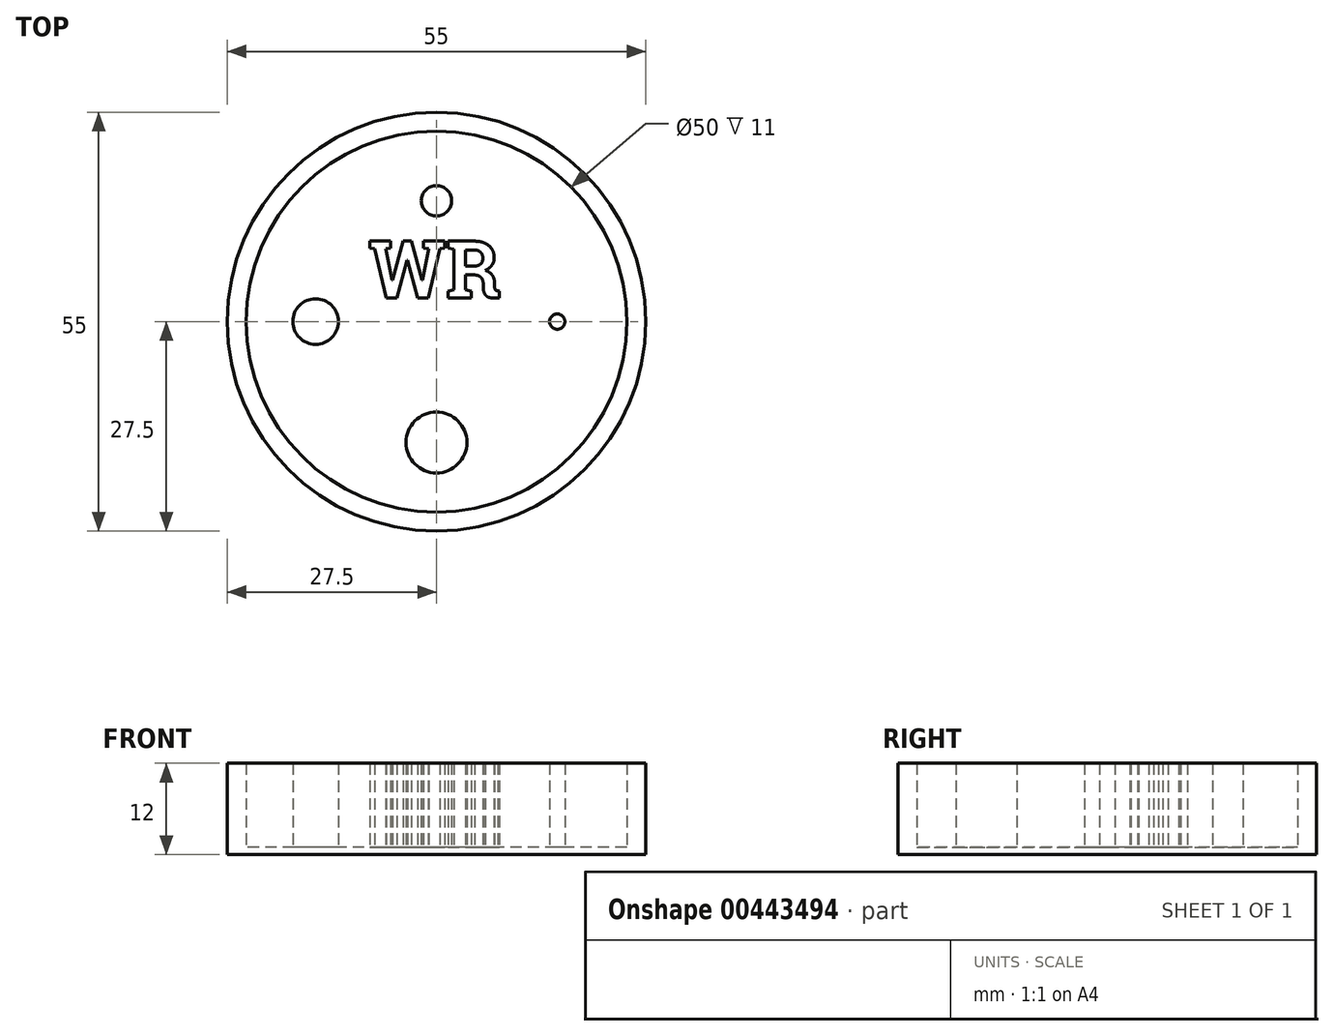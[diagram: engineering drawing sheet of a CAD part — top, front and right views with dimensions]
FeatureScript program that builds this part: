
annotation { "Feature Type Name" : "Feature", "Feature Type Description" : "" }
export const myFeature = defineFeature(function(context is Context, id is Id, definition is map)
    precondition{}
    {
        {
            var Q0;
            Q0=qCreatedBy(makeId("Top.planeOp"),FACE);
            var sketch = newSketch(context, id + "F0", { "sketchPlane" : qUnion([Q0])});
            skCircle(sketch, "E0", {"center": v(0, 0) * mm, "radius": 27.5 * mm});
            skCircle(sketch, "E1", {"center": v(0, 0) * mm, "radius": 25 * mm});
            skSolve(sketch);
        }
        {
            var Q0;
            Q0=qCreatedBy(makeId("Top.planeOp"),FACE);
            var sketch = newSketch(context, id + "F1", { "sketchPlane" : qUnion([Q0])});
            skText(sketch, "E2", { "text": "WR", "fontName": "RobotoSlab-Bold.ttf"});
            skCircle(sketch, "E3", {"center": v(-15.88, 0) * mm, "radius": 3 * mm});
            skCircle(sketch, "E4", {"center": v(0, -15.88) * mm, "radius": 4 * mm});
            skCircle(sketch, "E5", {"center": v(0, 15.88) * mm, "radius": 2 * mm});
            skCircle(sketch, "E6", {"center": v(15.88, 0) * mm, "radius": 1 * mm});
            const initialGuessF1  = {"E2": [-0.0089, 0.0031, 1, 0, 0.00757]};
            skSetInitialGuess(sketch, initialGuessF1);
            skSolve(sketch);
        }
        {
            var Q0;
            Q0=makeQuery(id+"F0.imprint","IMPRINT",FACE,{"disambiguationData":[TD([[makeQuery(id+"F0.imprint","IMPRINT",EDGE,{"derivedFrom":sQuery(id+"F0.wireOp",EDGE,"E1")}),1.0]])]});
            extrude(context, id + "F2", {"entities" : qUnion([Q0]), "depth" : 1 * mm});
        }
        {
            var Q0;
            Q0=makeQuery(id+"F0.imprint","IMPRINT",FACE,{"disambiguationData":[TD([[makeQuery(id+"F0.imprint","IMPRINT",EDGE,{"derivedFrom":sQuery(id+"F0.wireOp",EDGE,"E0")}),1.0]])]});
            extrude(context, id + "F3", {"entities" : qUnion([Q0]), "operationType" : NewBodyOperationType.ADD, "depth" : 12 * mm});
        }
        {
            var Q0;
            Q0 = qSketchRegion(id + "F1", true);
            extrude(context, id + "F4", {"entities" : qUnion([Q0]), "operationType" : NewBodyOperationType.ADD, "depth" : 12 * mm});
        }
    });
